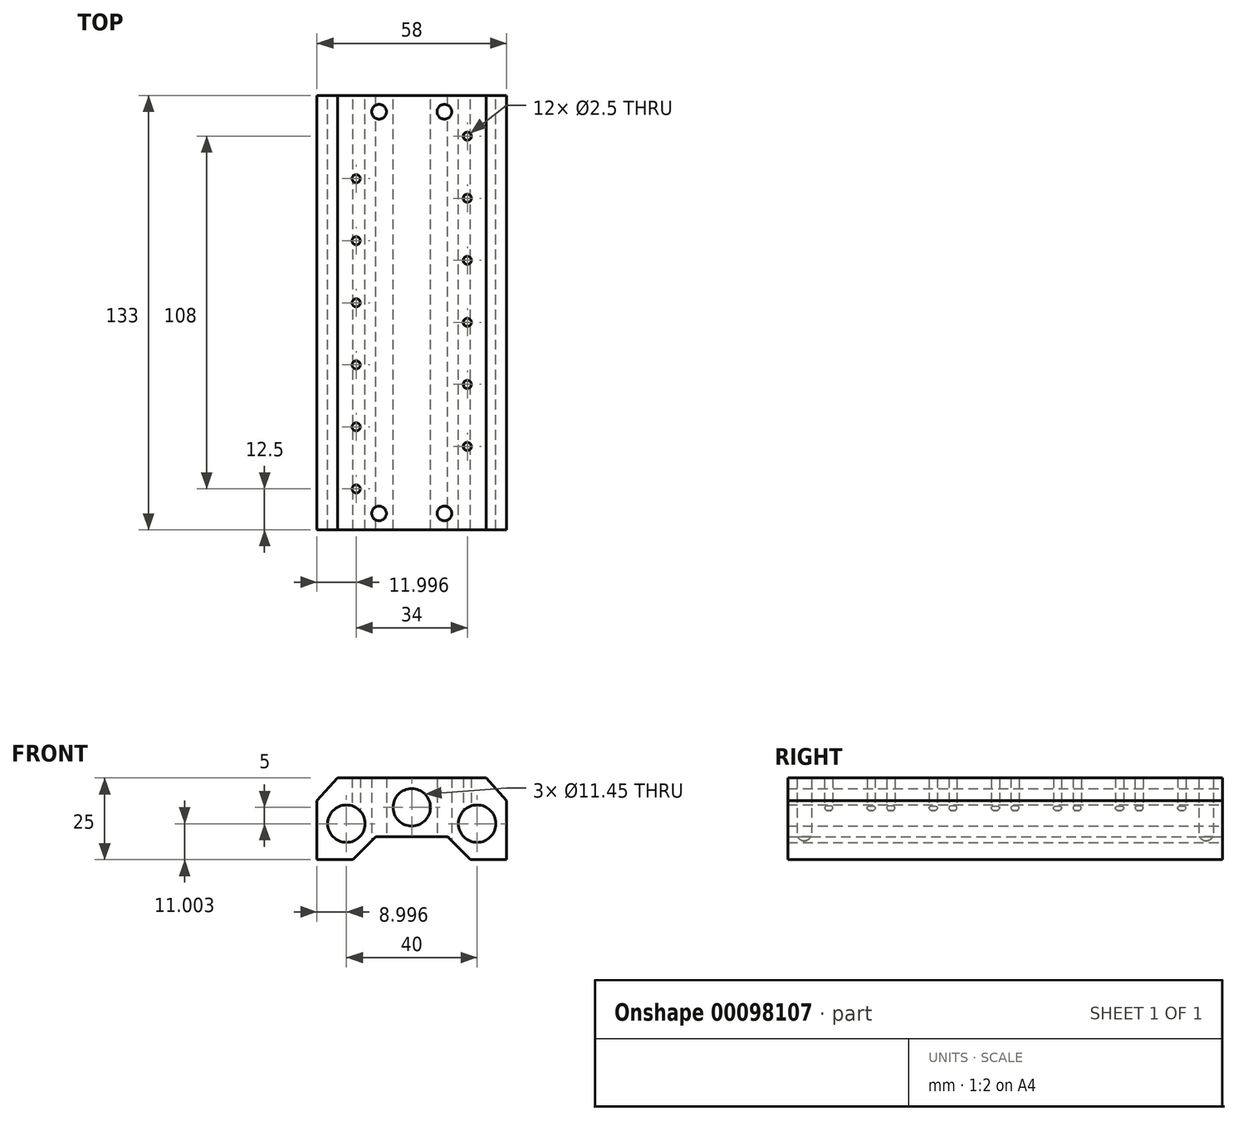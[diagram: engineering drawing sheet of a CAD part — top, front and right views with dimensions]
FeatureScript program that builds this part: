
annotation { "Feature Type Name" : "Feature", "Feature Type Description" : "" }
export const myFeature = defineFeature(function(context is Context, id is Id, definition is map)
    precondition{}
    {
        {
            var Q0;
            Q0=qCreatedBy(makeId("Front.planeOp"),FACE);
            var sketch = newSketch(context, id + "F0", { "sketchPlane" : qUnion([Q0])});
            skLineSegment(sketch, "E0", {"start": v(76.6, -101.1) * mm, "end": v(-76.6, -101.1) * mm});
            skLineSegment(sketch, "E1", {"start": v(76.6, -124.14) * mm, "end": v(-76.6, -124.14) * mm});
            skLineSegment(sketch, "E2", {"start": v(-25.9, -124.14) * mm, "end": v(-25.9, -101.1) * mm});
            skLineSegment(sketch, "E3", {"start": v(-76.6, -124.14) * mm, "end": v(-76.6, -101.1) * mm});
            skLineSegment(sketch, "E4", {"start": v(-25.9, -105.7) * mm, "end": v(-59.7, -105.7) * mm});
            skLineSegment(sketch, "E5", {"start": v(-25.9, -110.32) * mm, "end": v(-59.7, -110.32) * mm});
            skLineSegment(sketch, "E6", {"start": v(-25.9, -114.92) * mm, "end": v(-76.6, -114.92) * mm});
            skLineSegment(sketch, "E7", {"start": v(-59.7, -114.92) * mm, "end": v(-59.7, -101.1) * mm});
            skLineSegment(sketch, "E8", {"start": v(-41.26, -114.92) * mm, "end": v(-41.26, -101.1) * mm});
            skCircle(sketch, "E9", {"center": v(-36.99, -108) * mm, "radius": 1.34 * mm});
            skCircle(sketch, "E10", {"center": v(-36.99, -108) * mm, "radius": 0.78 * mm});
            skLineSegment(sketch, "E11", {"start": v(-28.58, -109.34) * mm, "end": v(-28.58, -106.67) * mm});
            skLineSegment(sketch, "E12", {"start": v(-32.77, -108.8) * mm, "end": v(-32.77, -107.22) * mm});
            skLineSegment(sketch, "E13", {"start": v(-32.77, -107.22) * mm, "end": v(-28.58, -106.67) * mm});
            skLineSegment(sketch, "E14", {"start": v(-32.77, -108.8) * mm, "end": v(-28.58, -109.34) * mm});
            skLineSegment(sketch, "E15", {"start": v(-61.66, -113.5) * mm, "end": v(-62.7, -113.5) * mm});
            skLineSegment(sketch, "E16", {"start": v(-64.64, -113.67) * mm, "end": v(-63.6, -113.67) * mm});
            skLineSegment(sketch, "E17", {"start": v(-63.6, -113.67) * mm, "end": v(-64.64, -113.67) * mm});
            skCircle(sketch, "E18", {"center": v(-64.12, -113.67) * mm, "radius": 0.52 * mm});
            skLineSegment(sketch, "E19", {"start": v(-64.81, -113.67) * mm, "end": v(-63.43, -113.67) * mm});
            skLineSegment(sketch, "E20", {"start": v(-63.43, -113.67) * mm, "end": v(-64.81, -113.67) * mm});
            skLineSegment(sketch, "E21", {"start": v(-61.49, -114.53) * mm, "end": v(-61.49, -113.5) * mm});
            skLineSegment(sketch, "E22", {"start": v(-66.58, -113.5) * mm, "end": v(-67.62, -113.5) * mm});
            skLineSegment(sketch, "E23", {"start": v(-65.55, -113.5) * mm, "end": v(-66.59, -113.5) * mm});
            skLineSegment(sketch, "E24", {"start": v(-70.48, -113.5) * mm, "end": v(-71.51, -113.5) * mm});
            skLineSegment(sketch, "E25", {"start": v(-69.74, -113.67) * mm, "end": v(-68.36, -113.67) * mm});
            skLineSegment(sketch, "E26", {"start": v(-68.36, -113.67) * mm, "end": v(-69.74, -113.67) * mm});
            skLineSegment(sketch, "E27", {"start": v(-14.22, -119.53) * mm, "end": v(-14.22, -124.14) * mm});
            skLineSegment(sketch, "E28", {"start": v(-14.22, -119.53) * mm, "end": v(-25.9, -119.53) * mm});
            skLineSegment(sketch, "E29", {"start": v(66.93, -113.77) * mm, "end": v(55.89, -113.77) * mm});
            skLineSegment(sketch, "E30", {"start": v(55.96, -110.31) * mm, "end": v(51.5, -110.31) * mm});
            skLineSegment(sketch, "E31", {"start": v(66.93, -122.22) * mm, "end": v(55.89, -122.22) * mm});
            skLineSegment(sketch, "E32", {"start": v(66.93, -113.77) * mm, "end": v(66.93, -122.25) * mm});
            skLineSegment(sketch, "E33", {"start": v(55.89, -113.77) * mm, "end": v(55.89, -122.22) * mm});
            skLineSegment(sketch, "E34", {"start": v(53.73, -110.31) * mm, "end": v(53.73, -112.04) * mm});
            skLineSegment(sketch, "E35", {"start": v(15.04, -110.31) * mm, "end": v(15.04, -113.77) * mm});
            skLineSegment(sketch, "E36", {"start": v(7.36, -113.77) * mm, "end": v(7.36, -122.22) * mm});
            skLineSegment(sketch, "E37", {"start": v(55.96, -103.4) * mm, "end": v(51.5, -103.4) * mm});
            skLineSegment(sketch, "E38", {"start": v(5.82, -103.4) * mm, "end": v(5.82, -110.31) * mm});
            skLineSegment(sketch, "E39", {"start": v(55.96, -103.4) * mm, "end": v(55.96, -110.31) * mm});
            skLineSegment(sketch, "E40", {"start": v(24.26, -103.4) * mm, "end": v(24.26, -110.31) * mm});
            skLineSegment(sketch, "E41", {"start": v(22.73, -113.77) * mm, "end": v(22.73, -122.22) * mm});
            skLineSegment(sketch, "E42", {"start": v(24.26, -103.4) * mm, "end": v(5.82, -103.4) * mm});
            skLineSegment(sketch, "E43", {"start": v(24.26, -110.31) * mm, "end": v(5.82, -110.31) * mm});
            skLineSegment(sketch, "E44", {"start": v(22.73, -113.77) * mm, "end": v(7.36, -113.77) * mm});
            skLineSegment(sketch, "E45", {"start": v(22.73, -122.22) * mm, "end": v(7.36, -122.22) * mm});
            skLineSegment(sketch, "E46", {"start": v(50.8, -103.4) * mm, "end": v(43.14, -103.4) * mm});
            skLineSegment(sketch, "E47", {"start": v(53.77, -113.77) * mm, "end": v(41.44, -113.77) * mm});
            skLineSegment(sketch, "E48", {"start": v(50.8, -110.31) * mm, "end": v(43.14, -110.31) * mm});
            skLineSegment(sketch, "E49", {"start": v(53.77, -122.22) * mm, "end": v(41.44, -122.22) * mm});
            skLineSegment(sketch, "E50", {"start": v(43.14, -103.4) * mm, "end": v(43.14, -110.31) * mm});
            skLineSegment(sketch, "E51", {"start": v(41.44, -113.77) * mm, "end": v(41.44, -122.22) * mm});
            skLineSegment(sketch, "E52", {"start": v(50.8, -103.4) * mm, "end": v(50.8, -110.31) * mm});
            skLineSegment(sketch, "E53", {"start": v(53.77, -113.77) * mm, "end": v(53.77, -122.22) * mm});
            skLineSegment(sketch, "E54", {"start": v(25.45, -106.88) * mm, "end": v(28.5, -106.88) * mm});
            skLineSegment(sketch, "E55", {"start": v(39.65, -106.88) * mm, "end": v(42.7, -106.88) * mm});
            skLineSegment(sketch, "E56", {"start": v(51.5, -103.4) * mm, "end": v(51.5, -110.31) * mm});
            skLineSegment(sketch, "E57", {"start": v(48.65, -113.77) * mm, "end": v(48.65, -110.31) * mm});
            skLineSegment(sketch, "E58", {"start": v(53.73, -112.04) * mm, "end": v(61.36, -112.04) * mm});
            skLineSegment(sketch, "E59", {"start": v(61.36, -113.77) * mm, "end": v(61.36, -112.04) * mm});
            skLineSegment(sketch, "E60", {"start": v(-49.6, -55.52) * mm, "end": v(-47.6, -55.52) * mm});
            skLineSegment(sketch, "E61", {"start": v(-48.6, -56.52) * mm, "end": v(-48.6, -54.52) * mm});
            skLineSegment(sketch, "E62", {"start": v(-29.6, -50.52) * mm, "end": v(-27.6, -50.52) * mm});
            skLineSegment(sketch, "E63", {"start": v(-28.6, -51.52) * mm, "end": v(-28.6, -49.52) * mm});
            skLineSegment(sketch, "E64", {"start": v(-9.6, -55.52) * mm, "end": v(-7.6, -55.52) * mm});
            skLineSegment(sketch, "E65", {"start": v(-8.6, -56.52) * mm, "end": v(-8.6, -54.52) * mm});
            skLineSegment(sketch, "E66", {"start": v(-46.6, -2.36) * mm, "end": v(-44.6, -2.36) * mm});
            skLineSegment(sketch, "E67", {"start": v(-45.6, -3.36) * mm, "end": v(-45.6, -1.36) * mm});
            skLineSegment(sketch, "E68", {"start": v(-48.45, -2.36) * mm, "end": v(-47.4, -2.36) * mm});
            skLineSegment(sketch, "E69", {"start": v(-43.8, -2.36) * mm, "end": v(-42.75, -2.36) * mm});
            skLineSegment(sketch, "E70", {"start": v(-45.6, -5.2) * mm, "end": v(-45.6, -4.16) * mm});
            skLineSegment(sketch, "E71", {"start": v(-45.6, -0.56) * mm, "end": v(-45.6, 0.5) * mm});
            skLineSegment(sketch, "E72", {"start": v(-46.6, 16.64) * mm, "end": v(-44.6, 16.64) * mm});
            skLineSegment(sketch, "E73", {"start": v(-45.6, 15.64) * mm, "end": v(-45.6, 17.64) * mm});
            skLineSegment(sketch, "E74", {"start": v(-48.45, 16.64) * mm, "end": v(-47.4, 16.64) * mm});
            skLineSegment(sketch, "E75", {"start": v(-43.8, 16.64) * mm, "end": v(-42.75, 16.64) * mm});
            skLineSegment(sketch, "E76", {"start": v(-45.6, 13.8) * mm, "end": v(-45.6, 14.84) * mm});
            skLineSegment(sketch, "E77", {"start": v(-45.6, 18.44) * mm, "end": v(-45.6, 19.5) * mm});
            skLineSegment(sketch, "E78", {"start": v(-12.6, 10.64) * mm, "end": v(-10.6, 10.64) * mm});
            skLineSegment(sketch, "E79", {"start": v(-11.6, 9.64) * mm, "end": v(-11.6, 11.64) * mm});
            skLineSegment(sketch, "E80", {"start": v(-14.45, 10.64) * mm, "end": v(-13.4, 10.64) * mm});
            skLineSegment(sketch, "E81", {"start": v(-9.8, 10.64) * mm, "end": v(-8.75, 10.64) * mm});
            skLineSegment(sketch, "E82", {"start": v(-11.6, 7.8) * mm, "end": v(-11.6, 8.84) * mm});
            skLineSegment(sketch, "E83", {"start": v(-11.6, 12.44) * mm, "end": v(-11.6, 13.5) * mm});
            skLineSegment(sketch, "E84", {"start": v(-12.6, 29.64) * mm, "end": v(-10.6, 29.64) * mm});
            skLineSegment(sketch, "E85", {"start": v(-11.6, 28.64) * mm, "end": v(-11.6, 30.64) * mm});
            skLineSegment(sketch, "E86", {"start": v(-14.45, 29.64) * mm, "end": v(-13.4, 29.64) * mm});
            skLineSegment(sketch, "E87", {"start": v(-9.8, 29.64) * mm, "end": v(-8.75, 29.64) * mm});
            skLineSegment(sketch, "E88", {"start": v(-11.6, 26.8) * mm, "end": v(-11.6, 27.84) * mm});
            skLineSegment(sketch, "E89", {"start": v(-11.6, 31.44) * mm, "end": v(-11.6, 32.5) * mm});
            skLineSegment(sketch, "E90", {"start": v(-39.6, -9.86) * mm, "end": v(-37.6, -9.86) * mm});
            skLineSegment(sketch, "E91", {"start": v(-38.6, -10.86) * mm, "end": v(-38.6, -8.86) * mm});
            skLineSegment(sketch, "E92", {"start": v(-42.45, -9.86) * mm, "end": v(-40.4, -9.86) * mm});
            skLineSegment(sketch, "E93", {"start": v(-36.8, -9.86) * mm, "end": v(-34.75, -9.86) * mm});
            skLineSegment(sketch, "E94", {"start": v(-38.6, -13.7) * mm, "end": v(-38.6, -11.66) * mm});
            skLineSegment(sketch, "E95", {"start": v(-38.6, -8.06) * mm, "end": v(-38.6, -6) * mm});
            skLineSegment(sketch, "E96", {"start": v(-19.6, -9.86) * mm, "end": v(-17.6, -9.86) * mm});
            skLineSegment(sketch, "E97", {"start": v(-18.6, -10.86) * mm, "end": v(-18.6, -8.86) * mm});
            skLineSegment(sketch, "E98", {"start": v(-22.45, -9.86) * mm, "end": v(-20.4, -9.86) * mm});
            skLineSegment(sketch, "E99", {"start": v(-16.8, -9.86) * mm, "end": v(-14.75, -9.86) * mm});
            skLineSegment(sketch, "E100", {"start": v(-18.6, -13.7) * mm, "end": v(-18.6, -11.66) * mm});
            skLineSegment(sketch, "E101", {"start": v(-18.6, -8.06) * mm, "end": v(-18.6, -6) * mm});
            skLineSegment(sketch, "E102", {"start": v(-39.6, 113.14) * mm, "end": v(-37.6, 113.14) * mm});
            skLineSegment(sketch, "E103", {"start": v(-38.6, 112.14) * mm, "end": v(-38.6, 114.14) * mm});
            skLineSegment(sketch, "E104", {"start": v(-42.45, 113.14) * mm, "end": v(-40.4, 113.14) * mm});
            skLineSegment(sketch, "E105", {"start": v(-36.8, 113.14) * mm, "end": v(-34.75, 113.14) * mm});
            skLineSegment(sketch, "E106", {"start": v(-38.6, 109.3) * mm, "end": v(-38.6, 111.34) * mm});
            skLineSegment(sketch, "E107", {"start": v(-38.6, 114.94) * mm, "end": v(-38.6, 117) * mm});
            skLineSegment(sketch, "E108", {"start": v(-19.6, 113.14) * mm, "end": v(-17.6, 113.14) * mm});
            skLineSegment(sketch, "E109", {"start": v(-18.6, 112.14) * mm, "end": v(-18.6, 114.14) * mm});
            skLineSegment(sketch, "E110", {"start": v(-22.45, 113.14) * mm, "end": v(-20.4, 113.14) * mm});
            skLineSegment(sketch, "E111", {"start": v(-16.8, 113.14) * mm, "end": v(-14.75, 113.14) * mm});
            skLineSegment(sketch, "E112", {"start": v(-18.6, 109.3) * mm, "end": v(-18.6, 111.34) * mm});
            skLineSegment(sketch, "E113", {"start": v(-18.6, 114.94) * mm, "end": v(-18.6, 117) * mm});
            skLineSegment(sketch, "E114", {"start": v(0.4, -48.52) * mm, "end": v(0.4, -66.52) * mm});
            skLineSegment(sketch, "E115", {"start": v(0.4, -66.52) * mm, "end": v(-10.6, -66.52) * mm});
            skLineSegment(sketch, "E116", {"start": v(-46.6, -66.52) * mm, "end": v(-57.6, -66.52) * mm});
            skLineSegment(sketch, "E117", {"start": v(-57.6, -66.52) * mm, "end": v(-57.6, -48.52) * mm});
            skLineSegment(sketch, "E118", {"start": v(-57.6, -48.52) * mm, "end": v(-51.35, -41.52) * mm});
            skLineSegment(sketch, "E119", {"start": v(-5.85, -41.52) * mm, "end": v(0.4, -48.52) * mm});
            skLineSegment(sketch, "E120", {"start": v(-17.6, -59.52) * mm, "end": v(-39.6, -59.52) * mm});
            skLineSegment(sketch, "E121", {"start": v(-10.6, -66.52) * mm, "end": v(-17.6, -59.52) * mm});
            skLineSegment(sketch, "E122", {"start": v(-39.6, -59.52) * mm, "end": v(-46.6, -66.52) * mm});
            skLineSegment(sketch, "E123", {"start": v(-51.35, -41.52) * mm, "end": v(-5.85, -41.52) * mm});
            skLineSegment(sketch, "E124", {"start": v(-57.6, 118.14) * mm, "end": v(-57.6, -14.86) * mm});
            skLineSegment(sketch, "E125", {"start": v(0.4, -14.86) * mm, "end": v(0.4, 118.14) * mm});
            skLineSegment(sketch, "E126", {"start": v(-57.6, -14.86) * mm, "end": v(-51.35, -14.86) * mm});
            skLineSegment(sketch, "E127", {"start": v(-5.85, -14.86) * mm, "end": v(0.4, -14.86) * mm});
            skLineSegment(sketch, "E128", {"start": v(-51.35, 118.14) * mm, "end": v(-57.6, 118.14) * mm});
            skLineSegment(sketch, "E129", {"start": v(0.4, 118.14) * mm, "end": v(-5.85, 118.14) * mm});
            skLineSegment(sketch, "E130", {"start": v(-51.35, -14.86) * mm, "end": v(-5.85, -14.86) * mm});
            skLineSegment(sketch, "E131", {"start": v(-51.35, -14.86) * mm, "end": v(-51.35, 118.14) * mm});
            skLineSegment(sketch, "E132", {"start": v(-5.85, 118.14) * mm, "end": v(-51.35, 118.14) * mm});
            skLineSegment(sketch, "E133", {"start": v(-5.85, 118.14) * mm, "end": v(-5.85, -14.86) * mm});
            skCircle(sketch, "E134", {"center": v(-38.6, -9.86) * mm, "radius": 2.25 * mm});
            skCircle(sketch, "E135", {"center": v(-18.6, -9.86) * mm, "radius": 2.25 * mm});
            skCircle(sketch, "E136", {"center": v(-38.6, 113.14) * mm, "radius": 2.25 * mm});
            skCircle(sketch, "E137", {"center": v(-18.6, 113.14) * mm, "radius": 2.25 * mm});
            skLineSegment(sketch, "E138", {"start": v(51.64, -14.86) * mm, "end": v(51.64, 118.14) * mm});
            skLineSegment(sketch, "E139", {"start": v(33.64, -14.86) * mm, "end": v(33.64, 118.14) * mm});
            skLineSegment(sketch, "E140", {"start": v(33.64, -14.86) * mm, "end": v(51.64, -14.86) * mm});
            skLineSegment(sketch, "E141", {"start": v(26.64, -14.86) * mm, "end": v(33.64, -14.86) * mm});
            skLineSegment(sketch, "E142", {"start": v(51.64, 118.14) * mm, "end": v(33.64, 118.14) * mm});
            skLineSegment(sketch, "E143", {"start": v(33.64, 118.14) * mm, "end": v(26.64, 118.14) * mm});
            skLineSegment(sketch, "E144", {"start": v(26.64, 118.14) * mm, "end": v(26.64, -14.86) * mm});
            skCircle(sketch, "E145", {"center": v(-48.6, -55.52) * mm, "radius": 5.72 * mm});
            skCircle(sketch, "E146", {"center": v(-28.6, -50.52) * mm, "radius": 5.72 * mm});
            skCircle(sketch, "E147", {"center": v(-8.6, -55.52) * mm, "radius": 5.72 * mm});
            skLineSegment(sketch, "E148", {"start": v(24.87, -76.56) * mm, "end": v(6.97, -76.56) * mm});
            skLineSegment(sketch, "E149", {"start": v(6.97, -76.56) * mm, "end": v(-1.71, -63.22) * mm});
            skLineSegment(sketch, "E150", {"start": v(11.4, -25.93) * mm, "end": v(-4.24, -25.93) * mm});
            skLineSegment(sketch, "E151", {"start": v(-4.24, -25.93) * mm, "end": v(-14.72, -14.24) * mm});
            skLineSegment(sketch, "E152", {"start": v(76.6, -124.14) * mm, "end": v(76.6, -101.1) * mm});
            skLineSegment(sketch, "E153", {"start": v(-28.6, -17.86) * mm, "end": v(-28.6, 121.14) * mm});
            skLineSegment(sketch, "E154", {"start": v(-46.6, 35.64) * mm, "end": v(-44.6, 35.64) * mm});
            skLineSegment(sketch, "E155", {"start": v(-45.6, 34.64) * mm, "end": v(-45.6, 36.64) * mm});
            skLineSegment(sketch, "E156", {"start": v(-48.45, 35.64) * mm, "end": v(-47.4, 35.64) * mm});
            skLineSegment(sketch, "E157", {"start": v(-43.8, 35.64) * mm, "end": v(-42.75, 35.64) * mm});
            skLineSegment(sketch, "E158", {"start": v(-45.6, 32.8) * mm, "end": v(-45.6, 33.84) * mm});
            skLineSegment(sketch, "E159", {"start": v(-45.6, 37.44) * mm, "end": v(-45.6, 38.5) * mm});
            skLineSegment(sketch, "E160", {"start": v(-46.6, 54.64) * mm, "end": v(-44.6, 54.64) * mm});
            skLineSegment(sketch, "E161", {"start": v(-45.6, 53.64) * mm, "end": v(-45.6, 55.64) * mm});
            skLineSegment(sketch, "E162", {"start": v(-48.45, 54.64) * mm, "end": v(-47.4, 54.64) * mm});
            skLineSegment(sketch, "E163", {"start": v(-43.8, 54.64) * mm, "end": v(-42.75, 54.64) * mm});
            skLineSegment(sketch, "E164", {"start": v(-45.6, 51.8) * mm, "end": v(-45.6, 52.84) * mm});
            skLineSegment(sketch, "E165", {"start": v(-45.6, 56.44) * mm, "end": v(-45.6, 57.5) * mm});
            skLineSegment(sketch, "E166", {"start": v(-12.6, 48.64) * mm, "end": v(-10.6, 48.64) * mm});
            skLineSegment(sketch, "E167", {"start": v(-11.6, 47.64) * mm, "end": v(-11.6, 49.64) * mm});
            skLineSegment(sketch, "E168", {"start": v(-14.45, 48.64) * mm, "end": v(-13.4, 48.64) * mm});
            skLineSegment(sketch, "E169", {"start": v(-9.8, 48.64) * mm, "end": v(-8.75, 48.64) * mm});
            skLineSegment(sketch, "E170", {"start": v(-11.6, 45.8) * mm, "end": v(-11.6, 46.84) * mm});
            skLineSegment(sketch, "E171", {"start": v(-11.6, 50.44) * mm, "end": v(-11.6, 51.5) * mm});
            skLineSegment(sketch, "E172", {"start": v(-12.6, 67.64) * mm, "end": v(-10.6, 67.64) * mm});
            skLineSegment(sketch, "E173", {"start": v(-11.6, 66.64) * mm, "end": v(-11.6, 68.64) * mm});
            skLineSegment(sketch, "E174", {"start": v(-14.45, 67.64) * mm, "end": v(-13.4, 67.64) * mm});
            skLineSegment(sketch, "E175", {"start": v(-9.8, 67.64) * mm, "end": v(-8.75, 67.64) * mm});
            skLineSegment(sketch, "E176", {"start": v(-11.6, 64.8) * mm, "end": v(-11.6, 65.84) * mm});
            skLineSegment(sketch, "E177", {"start": v(-11.6, 69.44) * mm, "end": v(-11.6, 70.5) * mm});
            skLineSegment(sketch, "E178", {"start": v(-46.6, 73.64) * mm, "end": v(-44.6, 73.64) * mm});
            skLineSegment(sketch, "E179", {"start": v(-45.6, 72.64) * mm, "end": v(-45.6, 74.64) * mm});
            skLineSegment(sketch, "E180", {"start": v(-48.45, 73.64) * mm, "end": v(-47.4, 73.64) * mm});
            skLineSegment(sketch, "E181", {"start": v(-43.8, 73.64) * mm, "end": v(-42.75, 73.64) * mm});
            skLineSegment(sketch, "E182", {"start": v(-45.6, 70.8) * mm, "end": v(-45.6, 71.84) * mm});
            skLineSegment(sketch, "E183", {"start": v(-45.6, 75.44) * mm, "end": v(-45.6, 76.5) * mm});
            skLineSegment(sketch, "E184", {"start": v(-46.6, 92.64) * mm, "end": v(-44.6, 92.64) * mm});
            skLineSegment(sketch, "E185", {"start": v(-45.6, 91.64) * mm, "end": v(-45.6, 93.64) * mm});
            skLineSegment(sketch, "E186", {"start": v(-48.45, 92.64) * mm, "end": v(-47.4, 92.64) * mm});
            skLineSegment(sketch, "E187", {"start": v(-43.8, 92.64) * mm, "end": v(-42.75, 92.64) * mm});
            skLineSegment(sketch, "E188", {"start": v(-45.6, 89.8) * mm, "end": v(-45.6, 90.84) * mm});
            skLineSegment(sketch, "E189", {"start": v(-45.6, 94.44) * mm, "end": v(-45.6, 95.5) * mm});
            skLineSegment(sketch, "E190", {"start": v(-12.6, 86.64) * mm, "end": v(-10.6, 86.64) * mm});
            skLineSegment(sketch, "E191", {"start": v(-11.6, 85.64) * mm, "end": v(-11.6, 87.64) * mm});
            skLineSegment(sketch, "E192", {"start": v(-14.45, 86.64) * mm, "end": v(-13.4, 86.64) * mm});
            skLineSegment(sketch, "E193", {"start": v(-9.8, 86.64) * mm, "end": v(-8.75, 86.64) * mm});
            skLineSegment(sketch, "E194", {"start": v(-11.6, 83.8) * mm, "end": v(-11.6, 84.84) * mm});
            skLineSegment(sketch, "E195", {"start": v(-11.6, 88.44) * mm, "end": v(-11.6, 89.5) * mm});
            skLineSegment(sketch, "E196", {"start": v(-12.6, 105.64) * mm, "end": v(-10.6, 105.64) * mm});
            skLineSegment(sketch, "E197", {"start": v(-11.6, 104.64) * mm, "end": v(-11.6, 106.64) * mm});
            skLineSegment(sketch, "E198", {"start": v(-14.45, 105.64) * mm, "end": v(-13.4, 105.64) * mm});
            skLineSegment(sketch, "E199", {"start": v(-9.8, 105.64) * mm, "end": v(-8.75, 105.64) * mm});
            skLineSegment(sketch, "E200", {"start": v(-11.6, 102.8) * mm, "end": v(-11.6, 103.84) * mm});
            skLineSegment(sketch, "E201", {"start": v(-11.6, 107.44) * mm, "end": v(-11.6, 108.5) * mm});
            skSolve(sketch);
        }
        {
            var Q0;
            {var subQ31=sQuery(id+"F0.wireOp",EDGE,"E115");Q0=makeQuery(id+"F0.imprint","IMPRINT",FACE,{"disambiguationData":[TD([[makeQuery(id+"F0.imprint","IMPRINT",EDGE,{"derivedFrom":subQ31}),-1.0]])]});}
            extrude(context, id + "F1", {"entities" : qUnion([Q0]), "depth" : 133 * mm});
        }
        {
            var Q0;
            Q0=makeQuery(id+"F1.opExtrude","SWEPT_FACE",FACE,{"disambiguationData":[OSD([sQuery(id+"F0.wireOp",EDGE,"E123")])]});
            var sketch = newSketch(context, id + "F2", { "sketchPlane" : qUnion([Q0])});
            skLineSegment(sketch, "E202.bottom", {"start": v(-38.6, -5) * mm, "end": v(-18.6, -5) * mm, "construction": true});
            skLineSegment(sketch, "E202.top", {"start": v(-38.6, -128) * mm, "end": v(-18.6, -128) * mm, "construction": true});
            skLineSegment(sketch, "E202.left", {"start": v(-38.6, -5) * mm, "end": v(-38.6, -128) * mm, "construction": true});
            skLineSegment(sketch, "E202.right", {"start": v(-18.6, -5) * mm, "end": v(-18.6, -128) * mm, "construction": true});
            skSolve(sketch);
        }
        {
            var Q0;
            Q0=sQuery(id+"F2.wireOp",VERTEX,"E202.left.start");
            var Q1;
            Q1=sQuery(id+"F2.wireOp",VERTEX,"E202.right.start");
            var Q2;
            Q2=sQuery(id+"F2.wireOp",VERTEX,"E202.top.end");
            var Q3;
            Q3=sQuery(id+"F2.wireOp",VERTEX,"E202.left.end");
            var Q4;
            Q4=makeQuery(id+"F1.opExtrude","SWEPT_BODY",BODY,{"disambiguationData":[OSD([sQuery(id+"F0.wireOp",EDGE,"E114"),sQuery(id+"F0.wireOp",EDGE,"E115"),sQuery(id+"F0.wireOp",EDGE,"E116"),sQuery(id+"F0.wireOp",EDGE,"E117"),sQuery(id+"F0.wireOp",EDGE,"E118"),sQuery(id+"F0.wireOp",EDGE,"E119"),sQuery(id+"F0.wireOp",EDGE,"E120"),sQuery(id+"F0.wireOp",EDGE,"E121"),sQuery(id+"F0.wireOp",EDGE,"E122"),sQuery(id+"F0.wireOp",EDGE,"E123"),sQuery(id+"F0.wireOp",EDGE,"E145"),sQuery(id+"F0.wireOp",EDGE,"E146"),sQuery(id+"F0.wireOp",EDGE,"E147")])]});
            hole(context, id + "F3", {"style" : HoleStyle.SIMPLE, "endStyle" : HoleEndStyle.THROUGH, "holeDiameter" : 4.5 * mm, "startFromSketch" : true, "locations" : qUnion([Q0, Q1, Q2, Q3]), "scope" : qUnion([Q4]), "isTappedThrough" : true});
        }
        {
            var Q0;
            Q0=makeQuery(id+"F1.opExtrude","SWEPT_FACE",FACE,{"disambiguationData":[OSD([sQuery(id+"F0.wireOp",EDGE,"E123")])]});
            var sketch = newSketch(context, id + "F4", { "sketchPlane" : qUnion([Q0])});
            skLineSegment(sketch, "E203", {"start": v(-28.6, 0) * mm, "end": v(-28.6, -133) * mm, "construction": true});
            skLineSegment(sketch, "E204", {"start": v(-45.6, -120.5) * mm, "end": v(-11.6, -107.5) * mm, "construction": true});
            skPoint(sketch, "E205", {"position": v(-28.6, -114) * mm});
            skLineSegment(sketch, "E206.0.1.0", {"start": v(-45.6, -101.5) * mm, "end": v(-11.6, -88.5) * mm, "construction": true});
            skLineSegment(sketch, "E206.0.2.0", {"start": v(-45.6, -82.5) * mm, "end": v(-11.6, -69.5) * mm, "construction": true});
            skLineSegment(sketch, "E206.0.3.0", {"start": v(-45.6, -63.5) * mm, "end": v(-11.6, -50.5) * mm, "construction": true});
            skLineSegment(sketch, "E206.0.4.0", {"start": v(-45.6, -44.5) * mm, "end": v(-11.6, -31.5) * mm, "construction": true});
            skLineSegment(sketch, "E206.0.5.0", {"start": v(-45.6, -25.5) * mm, "end": v(-11.6, -12.5) * mm, "construction": true});
            skLineSegment(sketch, "E206.direction1", {"start": v(-45.6, -120.5) * mm, "end": v(-20.6, -120.5) * mm, "construction": true});
            skLineSegment(sketch, "E206.direction2", {"start": v(-45.6, -120.5) * mm, "end": v(-45.6, -101.5) * mm, "construction": true});
            skSolve(sketch);
        }
        {
            var Q0;
            Q0=sQuery(id+"F4.wireOp",VERTEX,"E206.0.5.0.start");
            var Q1;
            Q1=sQuery(id+"F4.wireOp",VERTEX,"E206.0.5.0.end");
            var Q2;
            Q2=sQuery(id+"F4.wireOp",VERTEX,"E206.0.4.0.start");
            var Q3;
            Q3=sQuery(id+"F4.wireOp",VERTEX,"E206.0.4.0.end");
            var Q4;
            Q4=sQuery(id+"F4.wireOp",VERTEX,"E206.0.3.0.start");
            var Q5;
            Q5=sQuery(id+"F4.wireOp",VERTEX,"E206.0.3.0.end");
            var Q6;
            Q6=sQuery(id+"F4.wireOp",VERTEX,"E206.0.2.0.start");
            var Q7;
            Q7=sQuery(id+"F4.wireOp",VERTEX,"E206.0.2.0.end");
            var Q8;
            Q8=sQuery(id+"F4.wireOp",VERTEX,"E206.0.1.0.start");
            var Q9;
            Q9=sQuery(id+"F4.wireOp",VERTEX,"E206.0.1.0.end");
            var Q10;
            Q10=sQuery(id+"F4.wireOp",VERTEX,"E204.start");
            var Q11;
            Q11=sQuery(id+"F4.wireOp",VERTEX,"E204.end");
            var Q12;
            Q12=makeQuery(id+"F1.opExtrude","SWEPT_BODY",BODY,{"disambiguationData":[OSD([sQuery(id+"F0.wireOp",EDGE,"E114"),sQuery(id+"F0.wireOp",EDGE,"E115"),sQuery(id+"F0.wireOp",EDGE,"E116"),sQuery(id+"F0.wireOp",EDGE,"E117"),sQuery(id+"F0.wireOp",EDGE,"E118"),sQuery(id+"F0.wireOp",EDGE,"E119"),sQuery(id+"F0.wireOp",EDGE,"E120"),sQuery(id+"F0.wireOp",EDGE,"E121"),sQuery(id+"F0.wireOp",EDGE,"E122"),sQuery(id+"F0.wireOp",EDGE,"E123"),sQuery(id+"F0.wireOp",EDGE,"E145"),sQuery(id+"F0.wireOp",EDGE,"E146"),sQuery(id+"F0.wireOp",EDGE,"E147")])]});
            hole(context, id + "F5", {"style" : HoleStyle.SIMPLE, "endStyle" : HoleEndStyle.BLIND, "standardTappedOrClearance" : lookupTablePath({ "standard" : "ISO", "engagement" : "75%", "pitch" : "0.5 mm", "size" : "M3", "type" : "Tapped" }), "standardBlindInLast" : lookupTablePath({ "standard" : "ISO", "engagement" : "75%", "pitch" : "0.5 mm", "size" : "M3", "type" : "Tapped" }), "holeDiameter" : 2.5 * mm, "holeDepth" : 10 * mm, "startFromSketch" : true, "locations" : qUnion([Q0, Q1, Q2, Q3, Q4, Q5, Q6, Q7, Q8, Q9, Q10, Q11]), "scope" : qUnion([Q12]), "majorDiameter" : 3 * mm});
        }
    });
